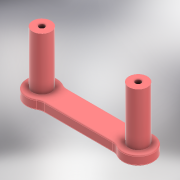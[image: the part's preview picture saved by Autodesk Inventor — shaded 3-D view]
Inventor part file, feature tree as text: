
AUTODESK INVENTOR PART (.ipt)
format: ipt  version: 2021 (Build 250183000, 183)  size: 395,264 bytes
history: native  units: mm
features: sketch x3, extrude x2, other x1, fillet x1, hole x1
ambient origin geometry x8: Origin, YZ Plane, XZ Plane, XY Plane, X Axis, Y Axis, Z Axis, Center Point
bodies: Body1 (feature_tree)
feature tree (8):
  other  "Sólido1"
  extrude  "Extrusão1"  Depth=3.0mm
  fillet  "Arredondamento1"  Radius=2.5mm
  extrude  "Extrusão2"  Depth=25.0mm
  hole  "Furo1"  [1 undecoded]
  sketch  "Esboço1"  dims[d3=6.0mm d5=3.0mm d7=2.5mm d8=0.0mm]
  sketch  "Esboço2"  dims[d9=0.3mm d11=25.0mm]
  sketch  "Esboço3"  dims[d13=4.0mm d14=4.8mm d15=13.7mm d16=0.0mm d17=1.5mm d18=6.0mm d19=4.0mm d20=2.0mm d21=90.0deg d22=10.0mm d23=20.594885mm]
note: 1 required parameter value undecoded (feature->parameter linkage not recoverable at this tier; creation-order binding heuristic only, values carry confidence <= 0.55)
